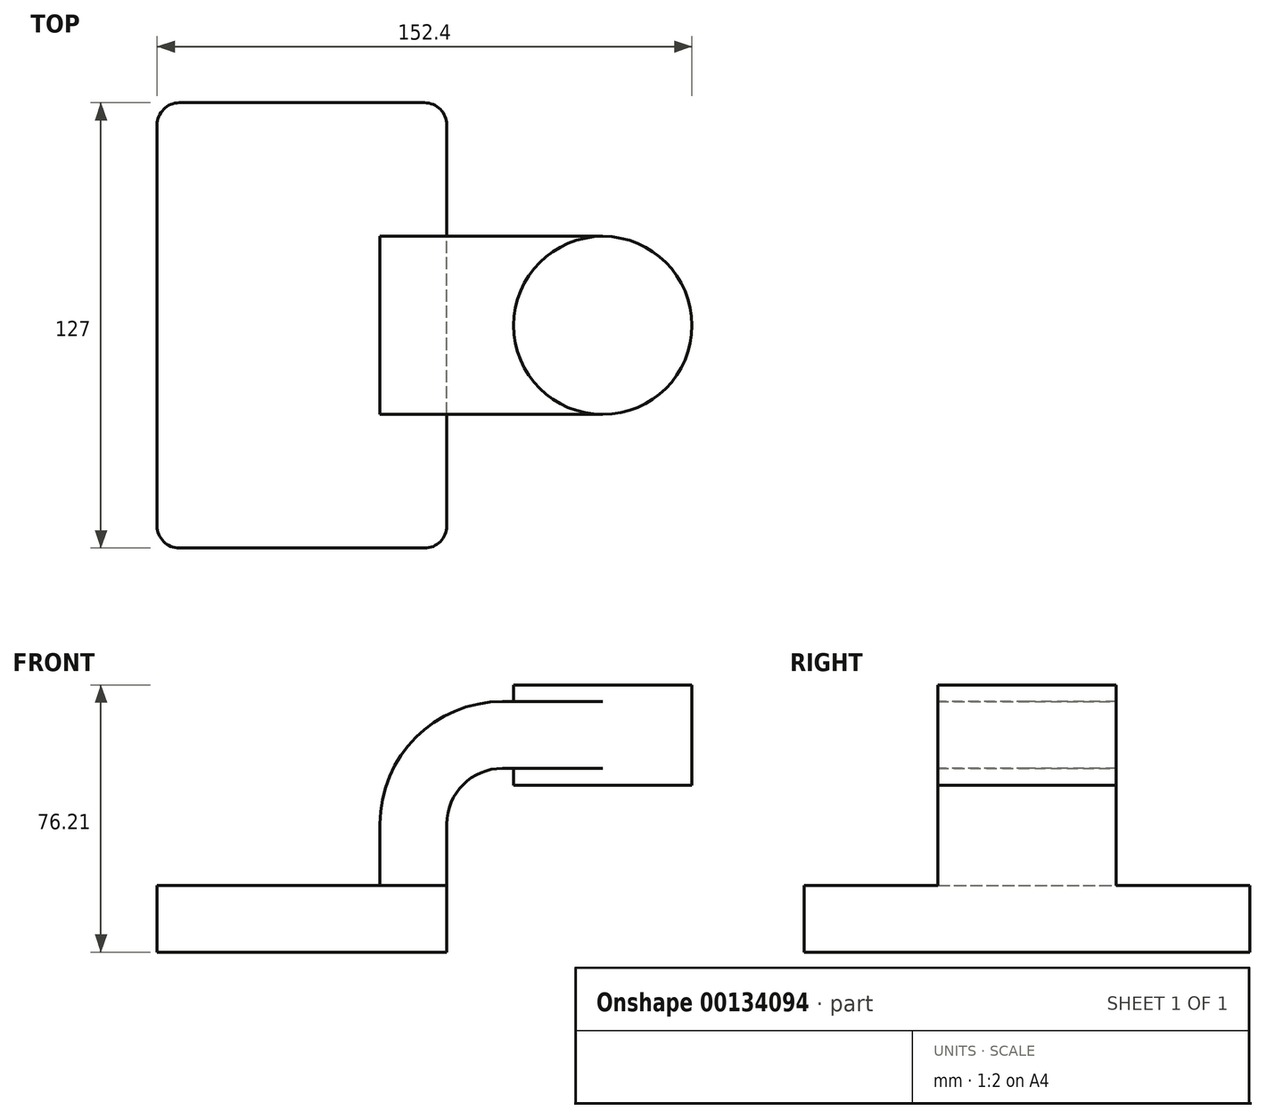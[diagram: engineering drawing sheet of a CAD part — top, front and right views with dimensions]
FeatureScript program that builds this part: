
annotation { "Feature Type Name" : "Feature", "Feature Type Description" : "" }
export const myFeature = defineFeature(function(context is Context, id is Id, definition is map)
    precondition{}
    {
        {
            var Q0;
            Q0=qCreatedBy(makeId("Front.planeOp"),FACE);
            var sketch = newSketch(context, id + "F0", { "sketchPlane" : qUnion([Q0])});
            skLineSegment(sketch, "E0.bottom", {"start": v(41.28, -9.52) * mm, "end": v(-41.28, -9.53) * mm});
            skLineSegment(sketch, "E0.top", {"start": v(41.28, 9.53) * mm, "end": v(-41.28, 9.53) * mm});
            skLineSegment(sketch, "E0.left", {"start": v(41.28, -9.52) * mm, "end": v(41.28, 9.53) * mm});
            skLineSegment(sketch, "E0.right", {"start": v(-41.28, -9.53) * mm, "end": v(-41.28, 9.53) * mm});
            skPoint(sketch, "E0.middle", {"position": v(0, 0) * mm});
            skLineSegment(sketch, "E1.bottom", {"start": v(60.33, 38.1) * mm, "end": v(111.12, 38.1) * mm});
            skLineSegment(sketch, "E1.top", {"start": v(60.32, 66.68) * mm, "end": v(111.12, 66.68) * mm});
            skLineSegment(sketch, "E1.left", {"start": v(60.33, 38.1) * mm, "end": v(60.32, 66.68) * mm});
            skLineSegment(sketch, "E1.right", {"start": v(111.12, 38.1) * mm, "end": v(111.12, 66.68) * mm});
            skPoint(sketch, "E1.middle", {"position": v(85.72, 52.39) * mm});
            skLineSegment(sketch, "E2", {"start": v(41.28, 9.53) * mm, "end": v(41.28, 27) * mm});
            skArc(sketch, "E3", {"start": v(41.27, 27) * mm, "mid": v(45.92, 38.23) * mm, "end": v(57.15, 42.88) * mm});
            skLineSegment(sketch, "E4", {"start": v(57.15, 42.88) * mm, "end": v(70.07, 42.88) * mm});
            skLineSegment(sketch, "E5.0", {"start": v(57.15, 61.93) * mm, "end": v(70.07, 61.93) * mm});
            skArc(sketch, "E5.1", {"start": v(22.23, 27) * mm, "mid": v(32.45, 51.7) * mm, "end": v(57.15, 61.93) * mm});
            skLineSegment(sketch, "E5.2", {"start": v(22.22, 9.53) * mm, "end": v(22.22, 27) * mm});
            skLineSegment(sketch, "E6", {"start": v(85.72, 38.1) * mm, "end": v(85.72, 66.68) * mm});
            skLineSegment(sketch, "E7", {"start": v(70.07, 61.93) * mm, "end": v(85.72, 61.93) * mm});
            skLineSegment(sketch, "E8", {"start": v(70.07, 42.88) * mm, "end": v(85.72, 42.88) * mm});
            skFitSpline(sketch, "E9", {"points": [v(-41.28, 9.53) * mm, v(57.15, 61.93) * mm], "startDerivative": vector(0.76, 86.64) * mm, "endDerivative": vector(123.45, -1) * mm});
            skSolve(sketch);
        }
        {
            var Q0;
            Q0=makeQuery(id+"F0.imprint","IMPRINT",FACE,{"disambiguationData":[TD([[makeQuery(id+"F0.imprint","IMPRINT",EDGE,{"derivedFrom":sQuery(id+"F0.wireOp",EDGE,"E0.bottom")}),-1.0]])]});
            extrude(context, id + "F1", {"entities" : qUnion([Q0]), "endBound" : BoundingType.SYMMETRIC, "depth" : 127 * mm});
        }
        {
            var Q0;
            {var subQ1=sQuery(id+"F0.wireOp",EDGE,"E2");Q0=makeQuery(id+"F0.imprint","IMPRINT",FACE,{"disambiguationData":[TD([[makeQuery(id+"F0.imprint","IMPRINT",EDGE,{"derivedFrom":subQ1}),1.0]])]});}
            var Q1;
            {var subQ0=sQuery(id+"F0.wireOp",EDGE,"E7");Q1=makeQuery(id+"F0.imprint","IMPRINT",FACE,{"disambiguationData":[TD([[makeQuery(id+"F0.imprint","IMPRINT",EDGE,{"derivedFrom":subQ0}),-1.0]])]});}
            extrude(context, id + "F2", {"entities" : qUnion([Q0, Q1]), "operationType" : NewBodyOperationType.ADD, "endBound" : BoundingType.SYMMETRIC, "depth" : 50.8 * mm});
        }
        {
            var Q0;
            Q0=makeQuery(id+"F0.imprint","IMPRINT",FACE,{"disambiguationData":[TD([[makeQuery(id+"F0.imprint","IMPRINT",EDGE,{"derivedFrom":sQuery(id+"F0.wireOp",EDGE,"E5.1")}),1.0]])]});
            extrude(context, id + "F3", {"entities" : qUnion([Q0]), "operationType" : NewBodyOperationType.ADD, "endBound" : BoundingType.SYMMETRIC, "depth" : 15.88 * mm});
        }
        {
            var Q0;
            {var subQ0=sQuery(id+"F0.wireOp",EDGE,"E1.right");Q0=makeQuery(id+"F0.imprint","IMPRINT",FACE,{"disambiguationData":[TD([[makeQuery(id+"F0.imprint","IMPRINT",EDGE,{"derivedFrom":subQ0}),1.0]])]});}
            var Q1;
            Q1=sQuery(id+"F0.wireOp",EDGE,"E6");
            revolve(context, id + "F4", {"operationType" : NewBodyOperationType.ADD, "entities" : qUnion([Q0]), "axis" : qUnion([Q1]), "revolveType" : RevolveType.FULL});
        }
        {
            var Q0;
            Q0=makeQuery(id+"F1.opExtrude","CAP_EDGE",EDGE,{"disambiguationData":[OSD([sQuery(id+"F0.wireOp",EDGE,"E0.left")])],"isStart":false});
            var Q1;
            Q1=makeQuery(id+"F1.opExtrude","CAP_EDGE",EDGE,{"disambiguationData":[OSD([sQuery(id+"F0.wireOp",EDGE,"E0.left")])],"isStart":true});
            var Q2;
            Q2=makeQuery(id+"F1.opExtrude","CAP_EDGE",EDGE,{"disambiguationData":[OSD([sQuery(id+"F0.wireOp",EDGE,"E0.right")])],"isStart":false});
            var Q3;
            Q3=makeQuery(id+"F1.opExtrude","CAP_EDGE",EDGE,{"disambiguationData":[OSD([sQuery(id+"F0.wireOp",EDGE,"E0.right")])],"isStart":true});
            fillet(context, id + "F5", {"entities" : qUnion([Q0, Q1, Q2, Q3]), "radius" : 6.35 * mm, "tangentPropagation" : true, "allowEdgeOverflow" : false});
        }
    });
